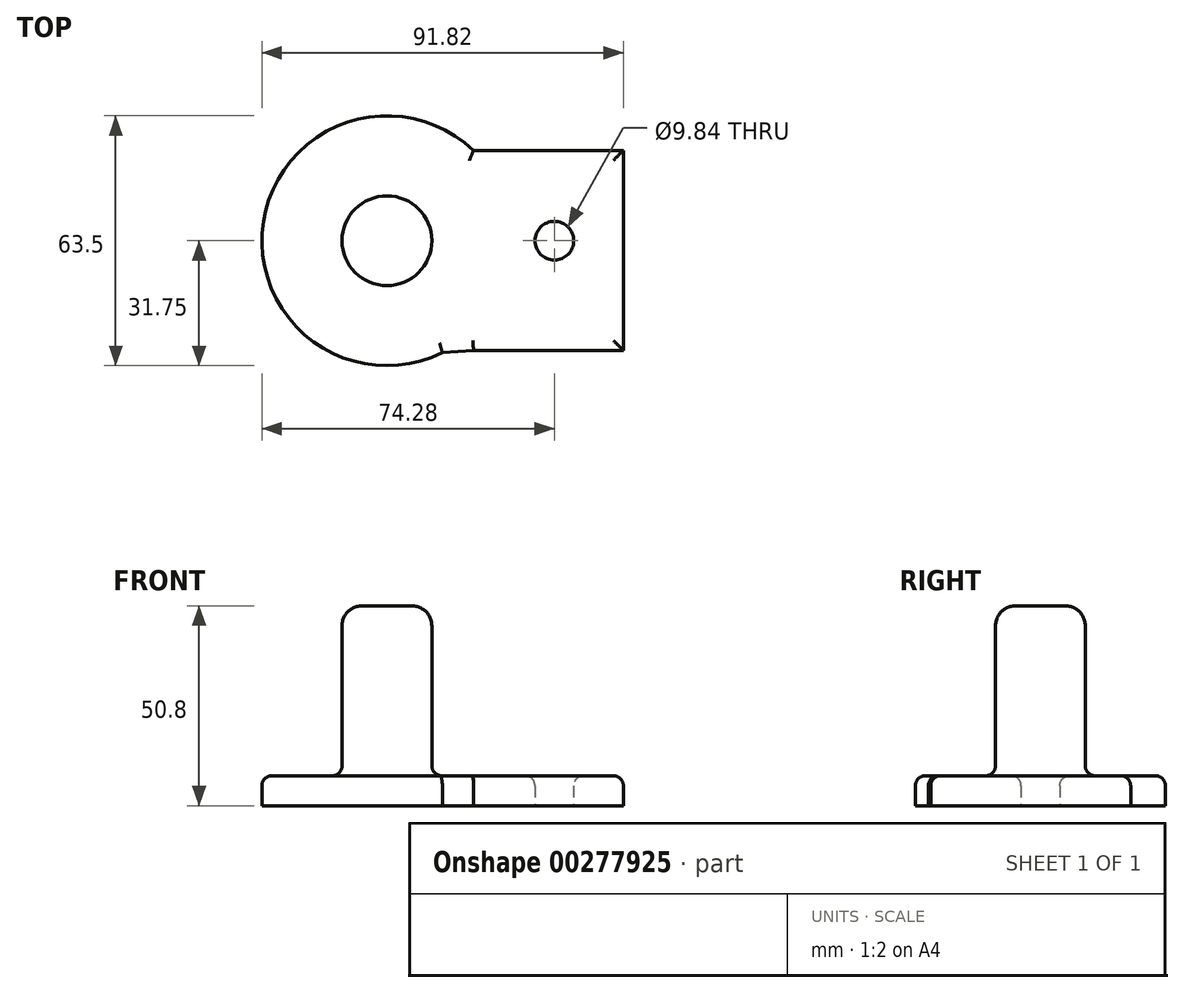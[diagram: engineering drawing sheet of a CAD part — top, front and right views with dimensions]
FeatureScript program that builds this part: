
annotation { "Feature Type Name" : "Feature", "Feature Type Description" : "" }
export const myFeature = defineFeature(function(context is Context, id is Id, definition is map)
    precondition{}
    {
        {
            var Q0;
            Q0=qCreatedBy(makeId("Top.planeOp"),FACE);
            var sketch = newSketch(context, id + "F0", { "sketchPlane" : qUnion([Q0])});
            skCircle(sketch, "E0", {"center": v(0, 0) * mm, "radius": 31.75 * mm});
            skCircle(sketch, "E1", {"center": v(0, 0) * mm, "radius": 11.4 * mm});
            skLineSegment(sketch, "E2.bottom", {"start": v(21.97, 22.92) * mm, "end": v(60.07, 22.92) * mm});
            skLineSegment(sketch, "E2.top", {"start": v(21.97, -27.88) * mm, "end": v(60.07, -27.88) * mm});
            skLineSegment(sketch, "E2.left", {"start": v(21.97, 22.92) * mm, "end": v(21.97, -27.88) * mm});
            skLineSegment(sketch, "E2.right", {"start": v(60.07, 22.92) * mm, "end": v(60.07, -27.88) * mm});
            skLineSegment(sketch, "E3", {"start": v(14.08, -28.46) * mm, "end": v(21.97, -27.88) * mm});
            skCircle(sketch, "E4", {"center": v(42.53, 0) * mm, "radius": 4.92 * mm});
            skSolve(sketch);
        }
        {
            var Q0;
            Q0=makeQuery(id+"F0.imprint","IMPRINT",FACE,{"disambiguationData":[TD([[makeQuery(id+"F0.imprint","IMPRINT",EDGE,{"derivedFrom":sQuery(id+"F0.wireOp",EDGE,"E1")}),1.0]])]});
            extrude(context, id + "F1", {"entities" : qUnion([Q0]), "depth" : 50.8 * mm});
        }
        {
            var Q0;
            Q0=makeQuery(id+"F1.opExtrude","CAP_FACE",FACE,{"disambiguationData":[OSD([sQuery(id+"F0.wireOp",EDGE,"E1")])],"isStart":false});
            fillet(context, id + "F2", {"entities" : qUnion([Q0]), "radius" : 5.08 * mm, "tangentPropagation" : true, "allowEdgeOverflow" : false});
        }
        {
            var Q0;
            Q0 = qSketchRegion(id + "F0", true);
            extrude(context, id + "F3", {"entities" : qUnion([Q0]), "operationType" : NewBodyOperationType.ADD, "depth" : 7.62 * mm});
        }
        {
            var Q0;
            Q0=makeQuery(id+"F3.opExtrude","CAP_FACE",FACE,{"disambiguationData":[OSD([sQuery(id+"F0.wireOp",EDGE,"E0"),sQuery(id+"F0.wireOp",EDGE,"E1"),sQuery(id+"F0.wireOp",EDGE,"E2.bottom"),sQuery(id+"F0.wireOp",EDGE,"E2.top"),sQuery(id+"F0.wireOp",EDGE,"E2.right"),sQuery(id+"F0.wireOp",EDGE,"E3")])],"isStart":false});
            fillet(context, id + "F4", {"entities" : qUnion([Q0]), "radius" : 2.54 * mm, "tangentPropagation" : true, "allowEdgeOverflow" : false});
        }
    });
